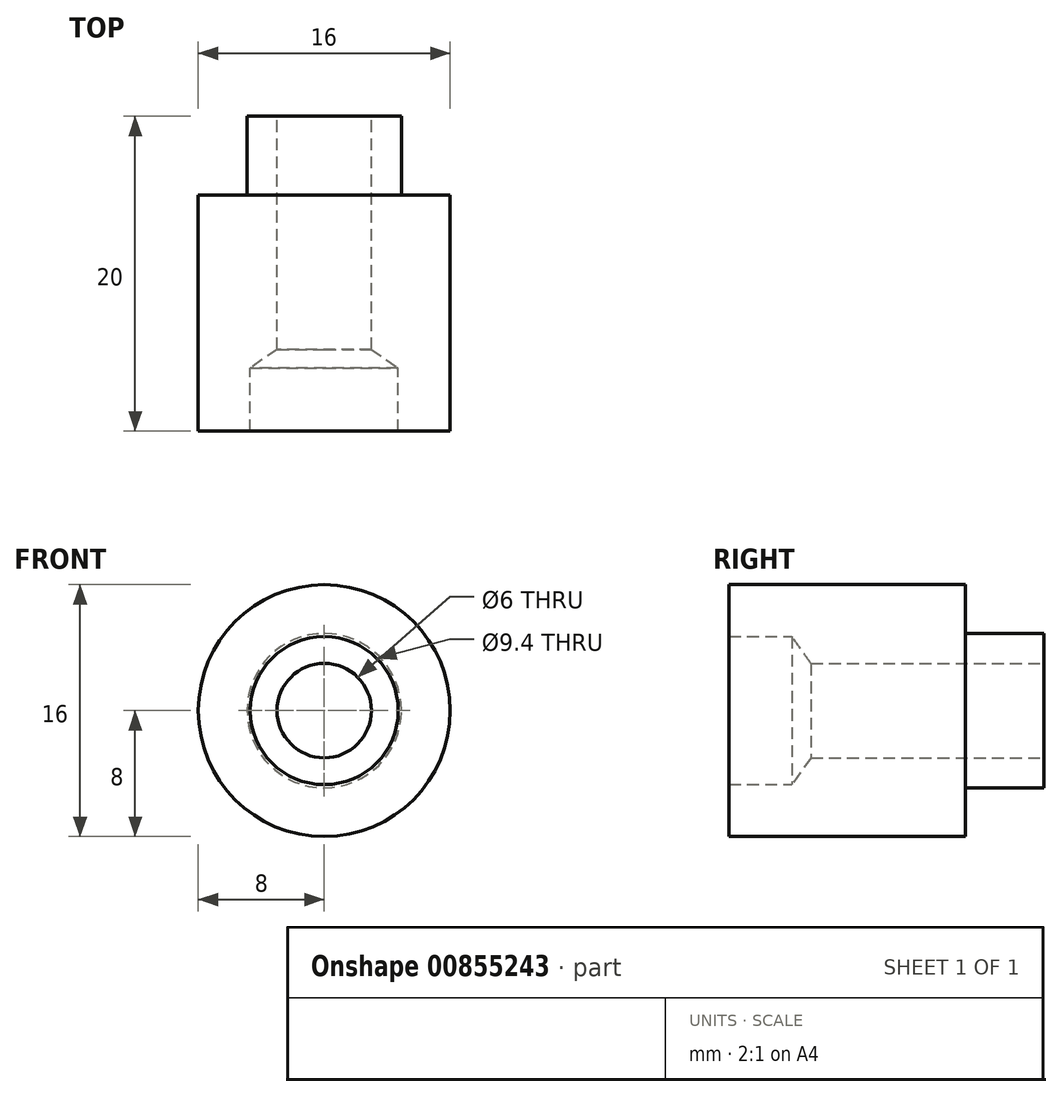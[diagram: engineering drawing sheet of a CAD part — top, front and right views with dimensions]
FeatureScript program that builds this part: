
annotation { "Feature Type Name" : "Feature", "Feature Type Description" : "" }
export const myFeature = defineFeature(function(context is Context, id is Id, definition is map)
    precondition{}
    {
        {
            var Q0;
            Q0=qCreatedBy(makeId("Right.planeOp"),FACE);
            var sketch = newSketch(context, id + "F0", { "sketchPlane" : qUnion([Q0])});
            skLineSegment(sketch, "E0", {"start": v(-15, 8) * mm, "end": v(-15, 4.7) * mm});
            skLineSegment(sketch, "E1", {"start": v(-15, 4.7) * mm, "end": v(-11, 4.7) * mm});
            skLineSegment(sketch, "E2", {"start": v(-9.8, 3) * mm, "end": v(5, 3) * mm});
            skLineSegment(sketch, "E3", {"start": v(5, 3) * mm, "end": v(5, 4.9) * mm});
            skLineSegment(sketch, "E4", {"start": v(5, 4.9) * mm, "end": v(0, 4.9) * mm});
            skLineSegment(sketch, "E5", {"start": v(0, 4.9) * mm, "end": v(0, 8) * mm});
            skLineSegment(sketch, "E6", {"start": v(0, 8) * mm, "end": v(-15, 8) * mm});
            skLineSegment(sketch, "E7", {"start": v(-11, 4.7) * mm, "end": v(-9.8, 3) * mm});
            skLineSegment(sketch, "E8", {"start": v(18.27, 0) * mm, "end": v(-25.21, 0) * mm, "construction": true});
            skSolve(sketch);
        }
        {
            var Q0;
            Q0 = qSketchRegion(id + "F0", true);
            var Q1;
            Q1=sQuery(id+"F0.wireOp",EDGE,"E8");
            revolve(context, id + "F1", {"surfaceOperationType" : NewSurfaceOperationType.NEW, "entities" : qUnion([Q0]), "axis" : qUnion([Q1]), "revolveType" : RevolveType.FULL});
        }
    });
